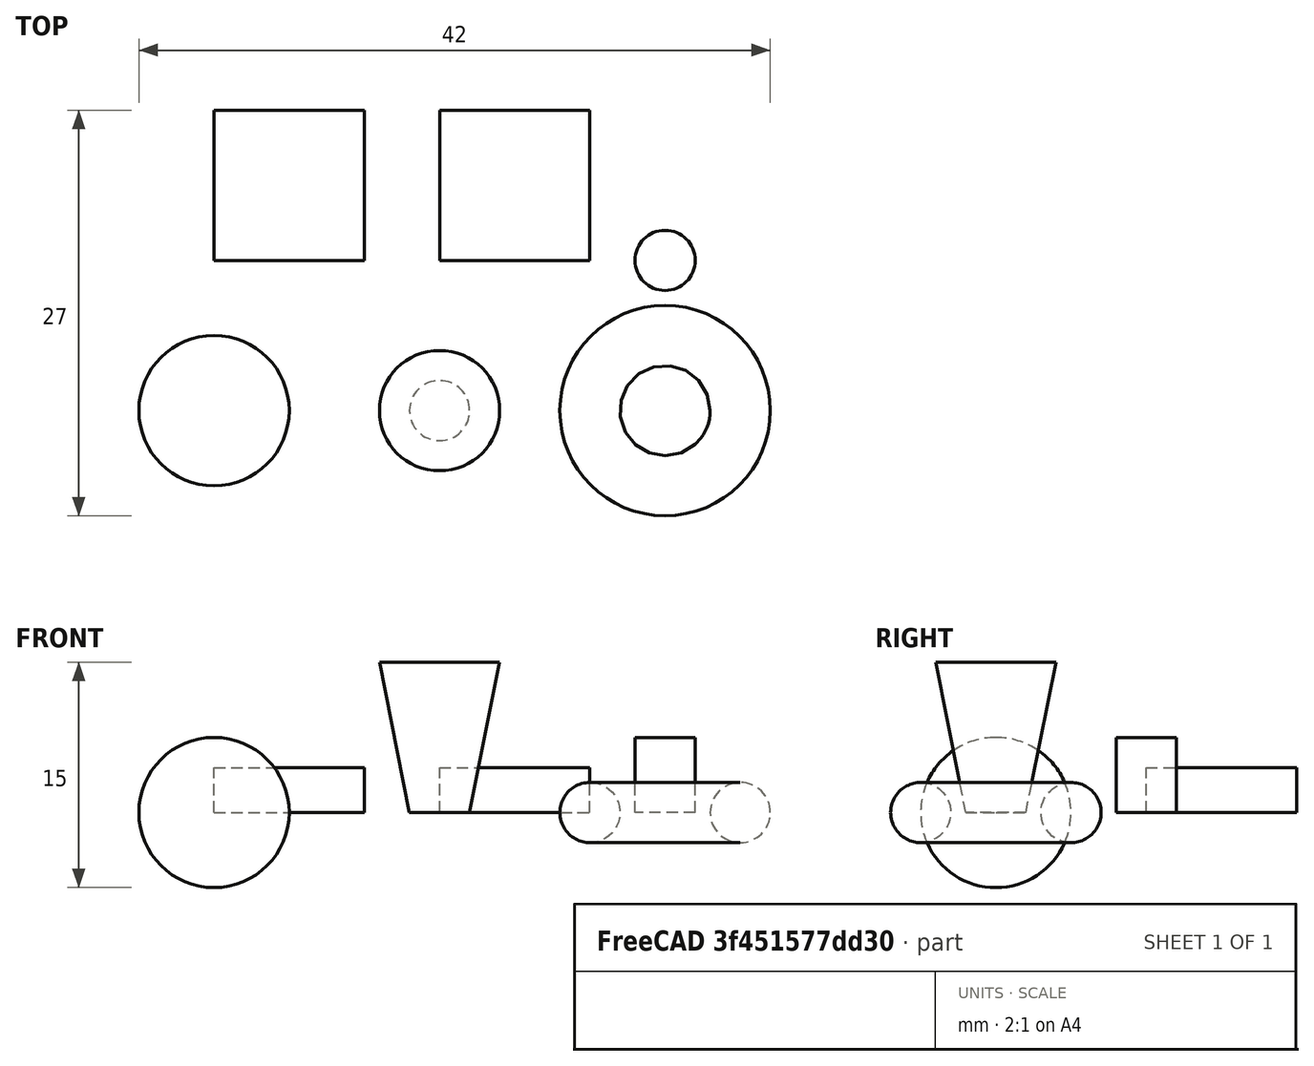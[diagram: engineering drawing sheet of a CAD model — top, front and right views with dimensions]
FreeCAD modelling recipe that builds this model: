
FCSTD DOCUMENT  (FreeCAD 0.16R6703 (Git))
Label: shapes-test
License: All rights reserved
LicenseURL: http://en.wikipedia.org/wiki/All_rights_reserved
objects: Part::Box×2, Part::Cylinder×1, Part::Sphere×1, Part::Cone×1, Part::Torus×1
note: 6 computed .brp shape members not serialized (recipe doc carries the construction recipe); baked Part::Feature solids carry a one-line shape summary decoded from their .brp

FEATURE [Part::Box] Box  label="Cube"
  Height = 3
  Length = 10
  Placement = pos=(15,0,0) rot=(0,0,1;0rad)
  Width = 10
FEATURE [Part::Box] Box001  label="Cube001"
  Height = 3
  Length = 10
  Width = 10
FEATURE [Part::Cylinder] Cylinder
  Angle = 360
  Height = 5
  Placement = pos=(30,0,0) rot=(0,0,1;0rad)
  Radius = 2
FEATURE [Part::Sphere] Sphere
  Angle1 = -90
  Angle2 = 90
  Angle3 = 360
  Placement = pos=(0,-10,0) rot=(0,0,1;0rad)
  Radius = 5
FEATURE [Part::Cone] Cone
  Angle = 360
  Height = 10
  Placement = pos=(15,-10,0) rot=(0,0,1;0rad)
  Radius1 = 2
  Radius2 = 4
FEATURE [Part::Torus] Torus
  Angle1 = -180
  Angle2 = 180
  Angle3 = 360
  Placement = pos=(30,-10,0) rot=(0,0,1;0rad)
  Radius1 = 5
  Radius2 = 2
